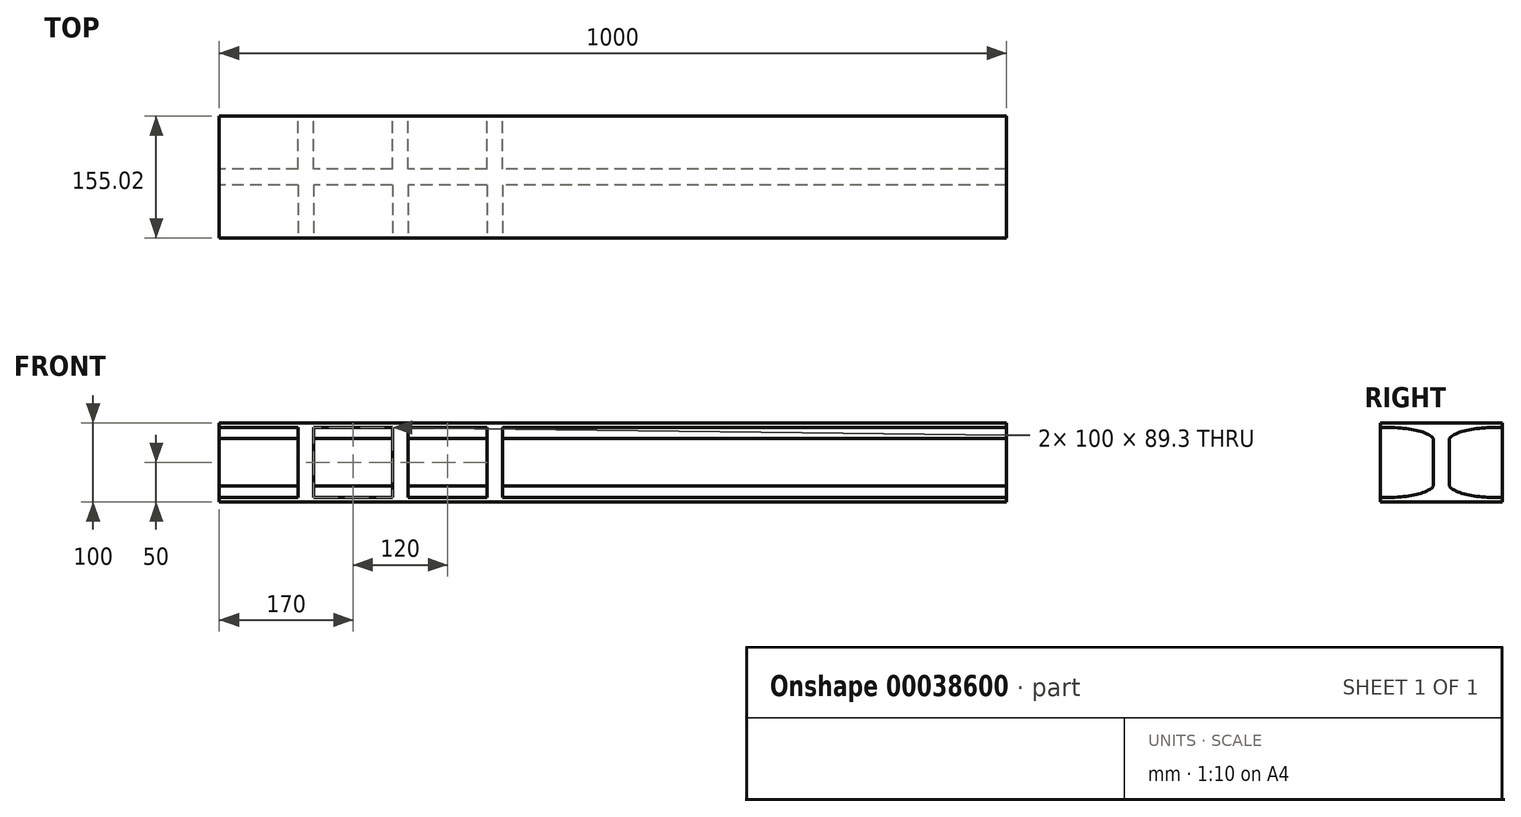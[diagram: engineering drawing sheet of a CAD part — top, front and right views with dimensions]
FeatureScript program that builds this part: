
annotation { "Feature Type Name" : "Feature", "Feature Type Description" : "" }
export const myFeature = defineFeature(function(context is Context, id is Id, definition is map)
    precondition{}
    {
        {
            var Q0;
            Q0=qCreatedBy(makeId("Right.planeOp"),FACE);
            var sketch = newSketch(context, id + "F0", { "sketchPlane" : qUnion([Q0])});
            skLineSegment(sketch, "E0.rect.bottom", {"start": v(77.5, 50) * mm, "end": v(-77.5, 50) * mm});
            skLineSegment(sketch, "E0.rect.top", {"start": v(77.5, -50) * mm, "end": v(-77.5, -50) * mm});
            skLineSegment(sketch, "E0.rect.left", {"start": v(77.5, 50) * mm, "end": v(77.5, -50) * mm, "construction": true});
            skLineSegment(sketch, "E0.rect.right", {"start": v(-77.5, 50) * mm, "end": v(-77.5, -50) * mm, "construction": true});
            skPoint(sketch, "E0.rect.middle", {"position": v(0, 0) * mm});
            skLineSegment(sketch, "E1", {"start": v(-10, -50) * mm, "end": v(-10, 50) * mm});
            skLineSegment(sketch, "E2", {"start": v(10, 50) * mm, "end": v(10, -50) * mm});
            skLineSegment(sketch, "E3", {"start": v(-10, 0) * mm, "end": v(0, 0) * mm, "construction": true});
            skLineSegment(sketch, "E4", {"start": v(0, 0) * mm, "end": v(10, 0) * mm, "construction": true});
            skFitSpline(sketch, "E5", {"points": [v(10, 30.17) * mm, v(30, 40.38) * mm, v(77.5, 44.65) * mm], "startDerivative": vector(26.02, 31.68) * mm, "endDerivative": vector(88.13, 0.07) * mm});
            skFitSpline(sketch, "E6.MirrorCS", {"points": [v(10, -30.17) * mm, v(30, -40.38) * mm, v(77.5, -44.65) * mm], "startDerivative": vector(26.02, -31.68) * mm, "endDerivative": vector(88.13, -0.07) * mm});
            skFitSpline(sketch, "E7.MirrorCS", {"points": [v(-10, -30.17) * mm, v(-30, -40.38) * mm, v(-77.5, -44.65) * mm], "startDerivative": vector(-26.02, -31.68) * mm, "endDerivative": vector(-88.13, -0.07) * mm});
            skFitSpline(sketch, "E8.MirrorCS", {"points": [v(-10, 30.17) * mm, v(-30, 40.38) * mm, v(-77.5, 44.65) * mm], "startDerivative": vector(-26.02, 31.68) * mm, "endDerivative": vector(-88.13, 0.07) * mm});
            skLineSegment(sketch, "E9", {"start": v(-77.5, 44.65) * mm, "end": v(-77.5, 50) * mm});
            skLineSegment(sketch, "E10", {"start": v(-77.5, -50) * mm, "end": v(-77.5, -44.65) * mm});
            skLineSegment(sketch, "E11", {"start": v(77.5, 44.65) * mm, "end": v(77.5, 50) * mm});
            skLineSegment(sketch, "E12", {"start": v(77.5, -50) * mm, "end": v(77.5, -44.65) * mm});
            skSolve(sketch);
        }
        {
            var Q0;
            {var subQ0=sQuery(id+"F0.wireOp",EDGE,"E8.MirrorCS");Q0=makeQuery(id+"F0.imprint","IMPRINT",FACE,{"disambiguationData":[TD([[makeQuery(id+"F0.imprint","IMPRINT",EDGE,{"derivedFrom":subQ0}),-1.0]])]});}
            var Q1;
            {var subQ5=sQuery(id+"F0.wireOp",EDGE,"E0.rect.bottom");var subQ7=sQuery(id+"F0.wireOp",EDGE,"E1");var subQ9=makeQuery(id+"F0.imprint","INTERSECT",VERTEX,{"derivedFrom":[subQ5,subQ7]});Q1=makeQuery(id+"F0.imprint","IMPRINT",FACE,{"disambiguationData":[TD([[makeQuery(id+"F0.imprint","IMPRINT",EDGE,{"disambiguationData":[TD([[subQ9,1.0]])],"derivedFrom":subQ5}),1.0]])]});}
            var Q2;
            {var subQ0=sQuery(id+"F0.wireOp",EDGE,"E5");Q2=makeQuery(id+"F0.imprint","IMPRINT",FACE,{"disambiguationData":[TD([[makeQuery(id+"F0.imprint","IMPRINT",EDGE,{"derivedFrom":subQ0}),1.0]])]});}
            var Q3;
            {var subQ1=sQuery(id+"F0.wireOp",EDGE,"E6.MirrorCS");Q3=makeQuery(id+"F0.imprint","IMPRINT",FACE,{"disambiguationData":[TD([[makeQuery(id+"F0.imprint","IMPRINT",EDGE,{"derivedFrom":subQ1}),-1.0]])]});}
            var Q4;
            {var subQ1=sQuery(id+"F0.wireOp",EDGE,"E7.MirrorCS");Q4=makeQuery(id+"F0.imprint","IMPRINT",FACE,{"disambiguationData":[TD([[makeQuery(id+"F0.imprint","IMPRINT",EDGE,{"derivedFrom":subQ1}),1.0]])]});}
            extrude(context, id + "F1", {"entities" : qUnion([Q0, Q1, Q2, Q3, Q4]), "endBound" : BoundingType.SYMMETRIC, "depth" : 1000 * mm});
        }
        {
            var Q0;
            Q0=makeQuery(id+"F1.opExtrude","SWEPT_FACE",FACE,{"disambiguationData":[OSD([sQuery(id+"F0.wireOp",EDGE,"E0.rect.bottom")])]});
            var sketch = newSketch(context, id + "F2", { "sketchPlane" : qUnion([Q0])});
            skLineSegment(sketch, "E13.bottom", {"start": v(-400, 77.5) * mm, "end": v(-380, 77.5) * mm});
            skLineSegment(sketch, "E13.top", {"start": v(-400, -77.5) * mm, "end": v(-380, -77.5) * mm});
            skLineSegment(sketch, "E13.left", {"start": v(-400, 77.5) * mm, "end": v(-400, -77.5) * mm});
            skLineSegment(sketch, "E13.right", {"start": v(-380, 77.5) * mm, "end": v(-380, -77.5) * mm});
            skLineSegment(sketch, "E14.bottom", {"start": v(-280, 77.5) * mm, "end": v(-260, 77.5) * mm});
            skLineSegment(sketch, "E14.top", {"start": v(-280, -77.5) * mm, "end": v(-260, -77.5) * mm});
            skLineSegment(sketch, "E14.left", {"start": v(-280, 77.5) * mm, "end": v(-280, -77.5) * mm});
            skLineSegment(sketch, "E14.right", {"start": v(-260, 77.5) * mm, "end": v(-260, -77.5) * mm});
            skLineSegment(sketch, "E15.bottom", {"start": v(-160, 77.5) * mm, "end": v(-140, 77.5) * mm});
            skLineSegment(sketch, "E15.top", {"start": v(-160, -77.5) * mm, "end": v(-140, -77.5) * mm});
            skLineSegment(sketch, "E15.left", {"start": v(-160, 77.5) * mm, "end": v(-160, -77.5) * mm});
            skLineSegment(sketch, "E15.right", {"start": v(-140, 77.5) * mm, "end": v(-140, -77.5) * mm});
            skSolve(sketch);
        }
        {
            var Q0;
            Q0=makeQuery(id+"F2.imprint","IMPRINT",FACE,{"disambiguationData":[TD([[makeQuery(id+"F2.imprint","IMPRINT",EDGE,{"derivedFrom":sQuery(id+"F2.wireOp",EDGE,"E13.bottom")}),1.0]])]});
            var Q1;
            Q1=makeQuery(id+"F2.imprint","IMPRINT",FACE,{"disambiguationData":[TD([[makeQuery(id+"F2.imprint","IMPRINT",EDGE,{"derivedFrom":sQuery(id+"F2.wireOp",EDGE,"E14.bottom")}),1.0]])]});
            var Q2;
            Q2=makeQuery(id+"F2.imprint","IMPRINT",FACE,{"disambiguationData":[TD([[makeQuery(id+"F2.imprint","IMPRINT",EDGE,{"derivedFrom":sQuery(id+"F2.wireOp",EDGE,"E15.bottom")}),1.0]])]});
            extrude(context, id + "F3", {"entities" : qUnion([Q0, Q1, Q2]), "operationType" : NewBodyOperationType.ADD, "oppositeDirection" : true, "depth" : 100 * mm});
        }
    });
